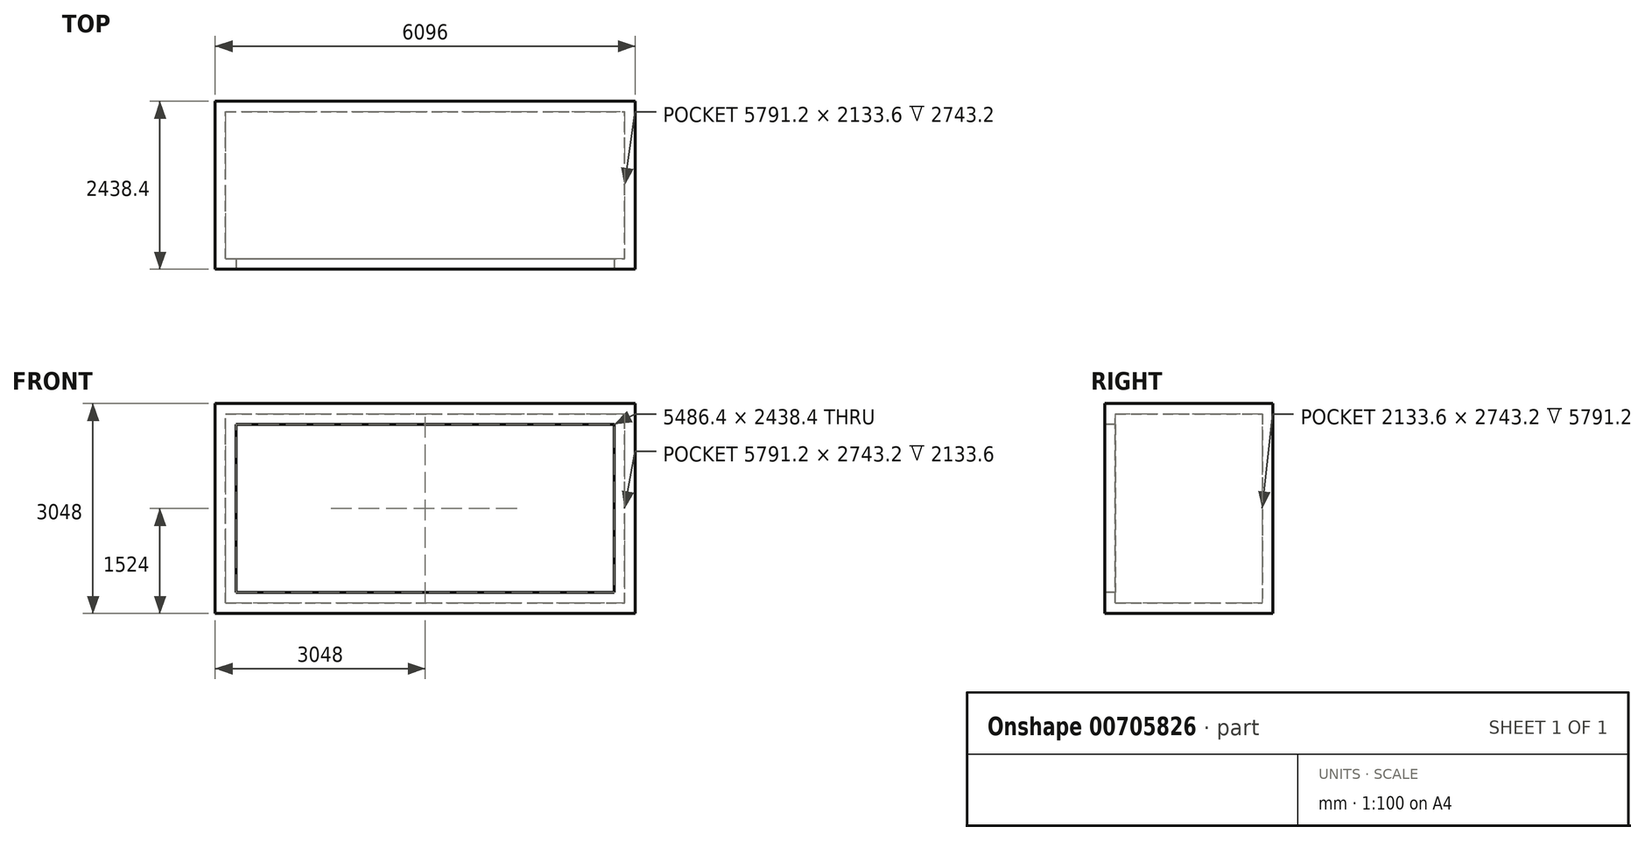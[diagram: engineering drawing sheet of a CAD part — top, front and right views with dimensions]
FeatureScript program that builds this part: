
annotation { "Feature Type Name" : "Feature", "Feature Type Description" : "" }
export const myFeature = defineFeature(function(context is Context, id is Id, definition is map)
    precondition{}
    {
        {
            var Q0;
            Q0=qCreatedBy(makeId("Top.planeOp"),FACE);
            var sketch = newSketch(context, id + "F0", { "sketchPlane" : qUnion([Q0])});
            skLineSegment(sketch, "E0.bottom", {"start": v(0, 0) * mm, "end": v(6096, 0) * mm});
            skLineSegment(sketch, "E0.top", {"start": v(0, 2438.4) * mm, "end": v(6096, 2438.4) * mm});
            skLineSegment(sketch, "E0.left", {"start": v(0, 0) * mm, "end": v(0, 2438.4) * mm});
            skLineSegment(sketch, "E0.right", {"start": v(6096, 0) * mm, "end": v(6096, 2438.4) * mm});
            skSolve(sketch);
        }
        {
            var Q0;
            Q0=makeQuery(id+"F0.imprint","IMPRINT",FACE,{"disambiguationData":[TD([[makeQuery(id+"F0.imprint","IMPRINT",EDGE,{"derivedFrom":sQuery(id+"F0.wireOp",EDGE,"E0.bottom")}),1.0]])]});
            extrude(context, id + "F1", {"entities" : qUnion([Q0]), "depth" : 3048 * mm, "offsetDistance" : 25.4 * mm});
        }
        {
            var Q0;
            Q0=makeQuery(id+"F1.opExtrude","SWEPT_FACE",FACE,{"disambiguationData":[OSD([sQuery(id+"F0.wireOp",EDGE,"E0.bottom")])]});
            var sketch = newSketch(context, id + "F2", { "sketchPlane" : qUnion([Q0])});
            skLineSegment(sketch, "E1.0.0", {"start": v(0, 0) * mm, "end": v(6096, 0) * mm});
            skLineSegment(sketch, "E1.0.1", {"start": v(6096, 0) * mm, "end": v(6096, 3048) * mm});
            skLineSegment(sketch, "E1.0.2", {"start": v(6096, 3048) * mm, "end": v(0, 3048) * mm});
            skLineSegment(sketch, "E1.0.3", {"start": v(0, 3048) * mm, "end": v(0, 0) * mm});
            skLineSegment(sketch, "E2.bottom", {"start": v(304.8, 2743.2) * mm, "end": v(5791.2, 2743.2) * mm});
            skLineSegment(sketch, "E2.top", {"start": v(304.8, 304.8) * mm, "end": v(5791.2, 304.8) * mm});
            skLineSegment(sketch, "E2.left", {"start": v(304.8, 2743.2) * mm, "end": v(304.8, 304.8) * mm});
            skLineSegment(sketch, "E2.right", {"start": v(5791.2, 2743.2) * mm, "end": v(5791.2, 304.8) * mm});
            skSolve(sketch);
        }
        {
            var Q0;
            Q0=makeQuery(id+"F1.opExtrude","SWEPT_FACE",FACE,{"disambiguationData":[OSD([sQuery(id+"F0.wireOp",EDGE,"E0.bottom")])]});
            shell(context, id + "F3", {"entities" : qUnion([Q0]), "thickness" : 152.4 * mm});
        }
        {
            var Q0;
            Q0=makeQuery(id+"F2.imprint","IMPRINT",FACE,{"disambiguationData":[TD([[makeQuery(id+"F2.imprint","IMPRINT",EDGE,{"derivedFrom":sQuery(id+"F2.wireOp",EDGE,"E1.0.0")}),1.0]])]});
            extrude(context, id + "F4", {"entities" : qUnion([Q0]), "operationType" : NewBodyOperationType.ADD, "oppositeDirection" : true, "depth" : 152.4 * mm, "offsetDistance" : 25.4 * mm});
        }
    });
